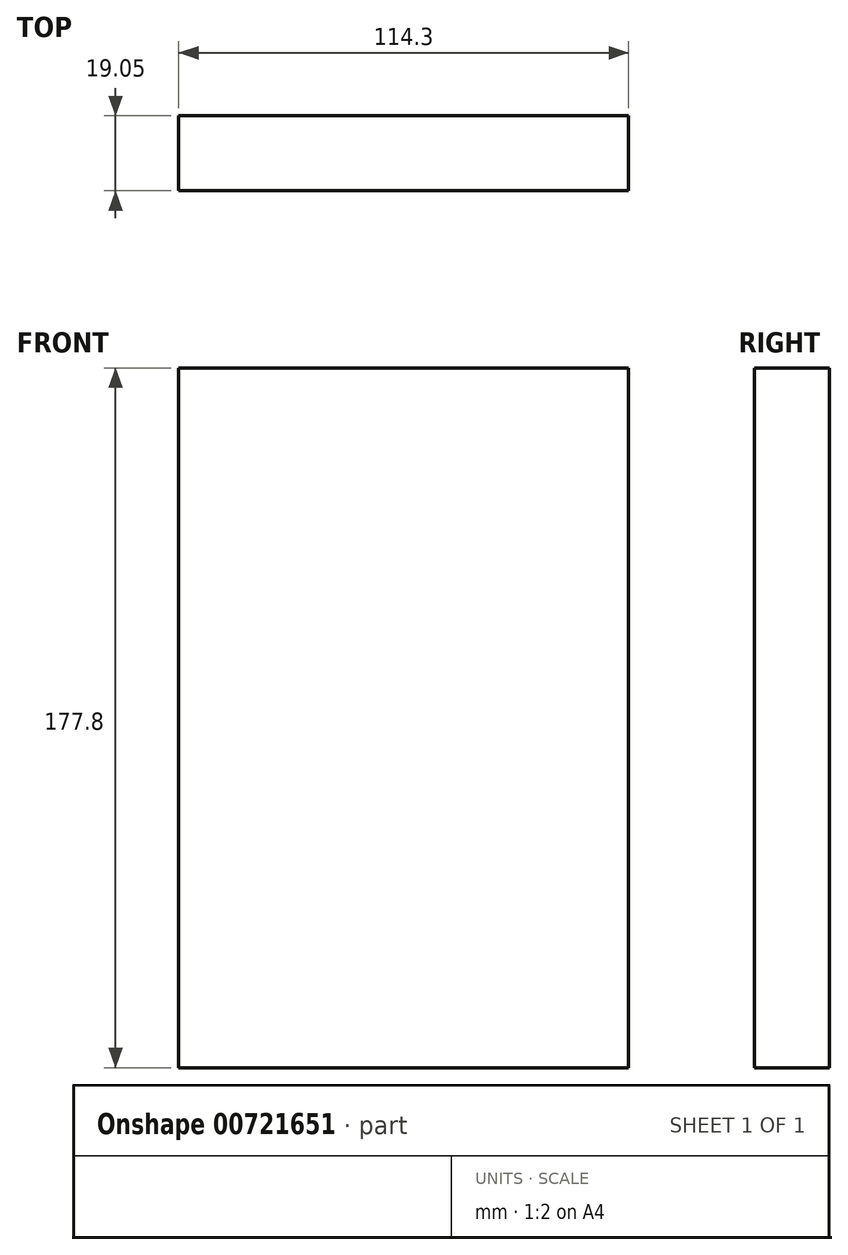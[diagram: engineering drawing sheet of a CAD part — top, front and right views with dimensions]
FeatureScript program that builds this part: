
annotation { "Feature Type Name" : "Feature", "Feature Type Description" : "" }
export const myFeature = defineFeature(function(context is Context, id is Id, definition is map)
    precondition{}
    {
        {
            var Q0;
            Q0=qCreatedBy(makeId("Front.planeOp"),FACE);
            var sketch = newSketch(context, id + "F0", { "sketchPlane" : qUnion([Q0])});
            skLineSegment(sketch, "E0.bottom", {"start": v(0, 0) * mm, "end": v(114.3, 0) * mm});
            skLineSegment(sketch, "E0.top", {"start": v(0, 177.8) * mm, "end": v(114.3, 177.8) * mm});
            skLineSegment(sketch, "E0.left", {"start": v(0, 0) * mm, "end": v(0, 177.8) * mm});
            skLineSegment(sketch, "E0.right", {"start": v(114.3, 0) * mm, "end": v(114.3, 177.8) * mm});
            skSolve(sketch);
        }
        {
            var Q0;
            Q0=makeQuery(id+"F0.imprint","IMPRINT",FACE,{"disambiguationData":[TD([[makeQuery(id+"F0.imprint","IMPRINT",EDGE,{"derivedFrom":sQuery(id+"F0.wireOp",EDGE,"E0.bottom")}),1.0]])]});
            extrude(context, id + "F1", {"entities" : qUnion([Q0]), "depth" : 19.05 * mm, "offsetDistance" : 25.4 * mm});
        }
    });
